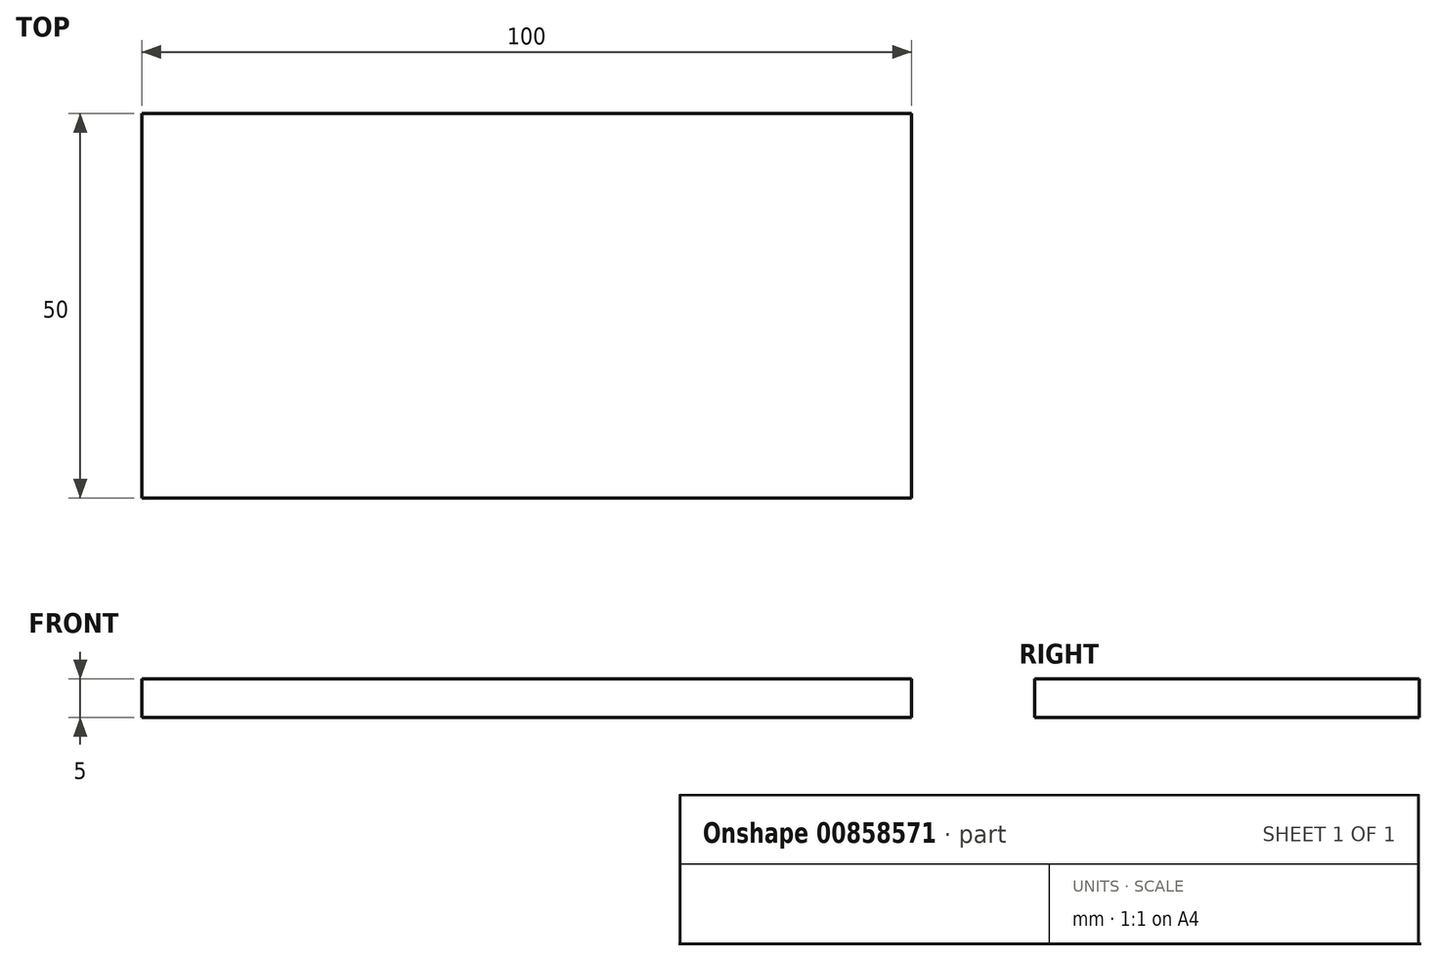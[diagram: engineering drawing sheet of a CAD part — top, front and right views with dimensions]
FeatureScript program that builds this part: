
annotation { "Feature Type Name" : "Feature", "Feature Type Description" : "" }
export const myFeature = defineFeature(function(context is Context, id is Id, definition is map)
    precondition{}
    {
        {
            var Q0;
            Q0=qCreatedBy(makeId("Top.planeOp"),FACE);
            var sketch = newSketch(context, id + "F0", { "sketchPlane" : qUnion([Q0])});
            skLineSegment(sketch, "E0.bottom", {"start": v(0, 0) * mm, "end": v(100, 0) * mm});
            skLineSegment(sketch, "E0.top", {"start": v(0, -50) * mm, "end": v(100, -50) * mm});
            skLineSegment(sketch, "E0.left", {"start": v(0, 0) * mm, "end": v(0, -50) * mm});
            skLineSegment(sketch, "E0.right", {"start": v(100, 0) * mm, "end": v(100, -50) * mm});
            skSolve(sketch);
        }
        {
            var Q0;
            Q0=makeQuery(id+"F0.imprint","IMPRINT",FACE,{"disambiguationData":[TD([[makeQuery(id+"F0.imprint","IMPRINT",EDGE,{"derivedFrom":sQuery(id+"F0.wireOp",EDGE,"E0.bottom")}),-1.0]])]});
            extrude(context, id + "F1", {"entities" : qUnion([Q0]), "depth" : 5 * mm, "offsetDistance" : 25 * mm});
        }
    });
